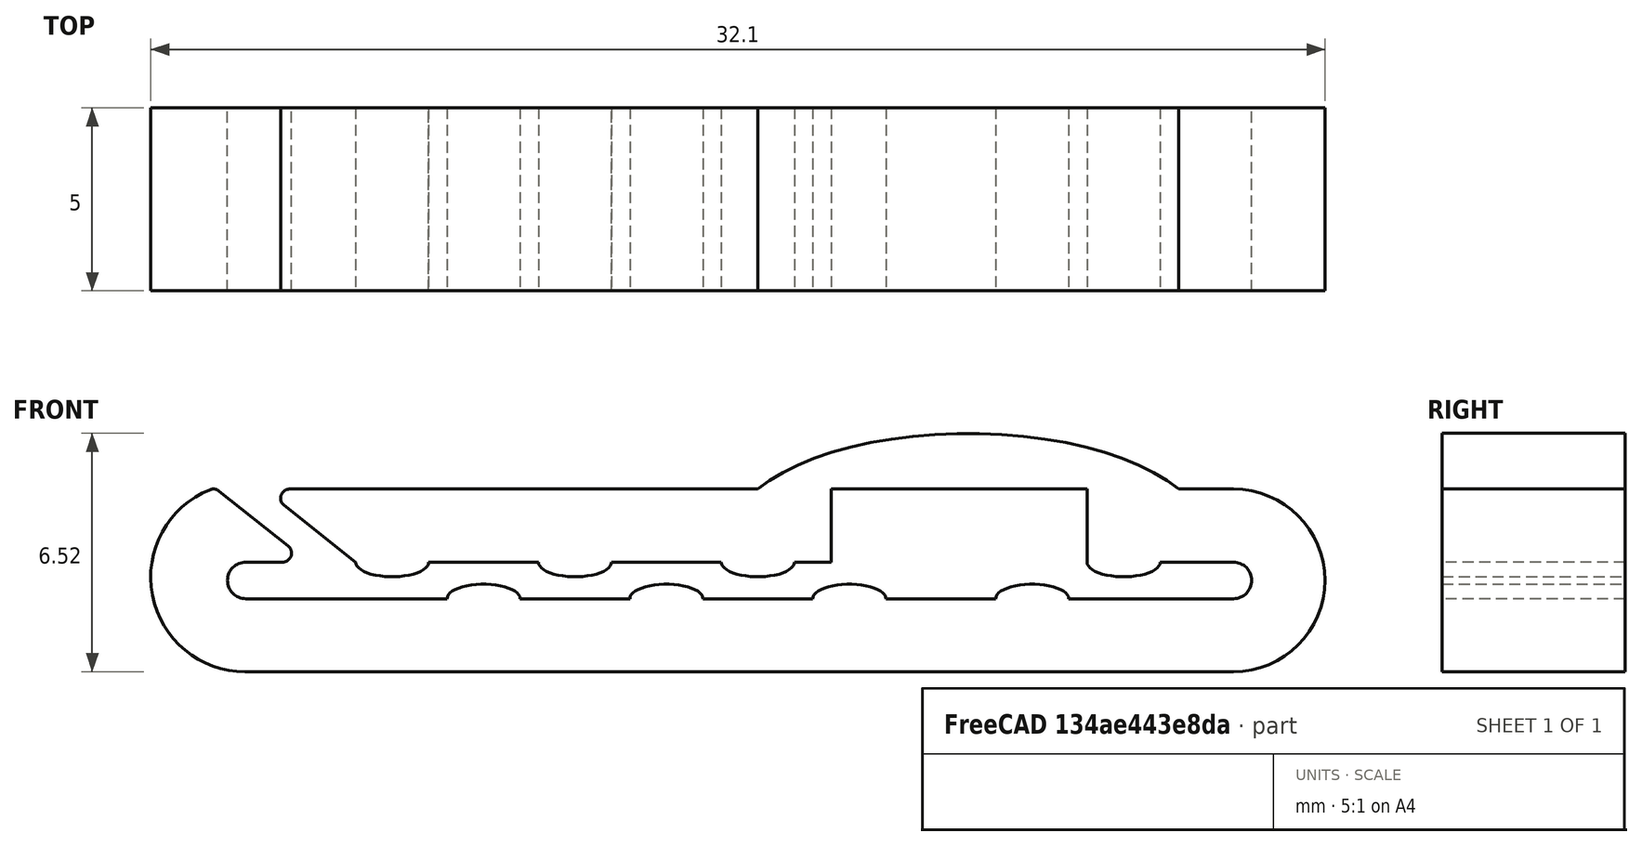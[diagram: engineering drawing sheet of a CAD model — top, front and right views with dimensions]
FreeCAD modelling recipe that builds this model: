
FCSTD DOCUMENT  (FreeCAD 2021.911R24301 +3846 (Git))
Label: BLTouch_Cable_Clamp
License: All rights reserved
LicenseURL: http://en.wikipedia.org/wiki/All_rights_reserved
objects: Sketcher::SketchObject×1, PartDesign::Pad×1, PartDesign::Body×1
note: 5 computed .brp shape members not serialized (recipe doc carries the construction recipe); baked Part::Feature solids carry a one-line shape summary decoded from their .brp

FEATURE [Sketcher::SketchObject] Sketch
  FullyConstrained = false
  MapMode = 5
  Placement = pos=(0,65.3,0) rot=(1,0,0;1.5708rad)
  sketch-geometry (56):
    g0: LineSegment StartX=62.4151 StartY=3.02512 StartZ=0 EndX=62.4151 EndY=5.02512 EndZ=0
    g1: LineSegment StartX=62.4151 StartY=5.02512 StartZ=0 EndX=55.4151 EndY=5.02512 EndZ=0
    g2: LineSegment StartX=55.4151 StartY=5.02512 StartZ=0 EndX=55.4151 EndY=3.02512 EndZ=0
    g3: LineSegment StartX=66.4151 StartY=2.02512 StartZ=0 EndX=61.9151 EndY=2.02512 EndZ=0
    g4: ArcOfEllipse CenterX=53.4151 CenterY=3.02512 CenterZ=0 NormalX=0 NormalY=0 NormalZ=1 MajorRadius=1 MinorRadius=0.4 AngleXU=-3.14159 StartAngle=0 EndAngle=3.14159
    g5: LineSegment [constr] StartX=52.4151 StartY=3.02512 StartZ=0 EndX=54.4151 EndY=3.02512 EndZ=0
    g6: LineSegment [constr] StartX=53.4151 StartY=2.62512 StartZ=0 EndX=53.4151 EndY=3.42512 EndZ=0
    g7: GeomPoint [constr] X=52.4986 Y=3.02512 Z=0
    g8: GeomPoint [constr] X=54.3317 Y=3.02512 Z=0
    g9: LineSegment StartX=55.4151 StartY=3.02512 StartZ=0 EndX=54.4151 EndY=3.02512 EndZ=0
    g10: ArcOfEllipse CenterX=60.9151 CenterY=2.02512 CenterZ=0 NormalX=0 NormalY=0 NormalZ=1 MajorRadius=1 MinorRadius=0.4 AngleXU=0 StartAngle=0 EndAngle=3.14159
    g11: LineSegment [constr] StartX=61.9151 StartY=2.02512 StartZ=0 EndX=59.9151 EndY=2.02512 EndZ=0
    g12: LineSegment [constr] StartX=60.9151 StartY=2.42512 StartZ=0 EndX=60.9151 EndY=1.62512 EndZ=0
    g13: GeomPoint [constr] X=61.8317 Y=2.02512 Z=0
    g14: GeomPoint [constr] X=59.9986 Y=2.02512 Z=0
    g15: ArcOfCircle CenterX=66.4151 CenterY=2.52512 CenterZ=0 NormalX=0 NormalY=0 NormalZ=1 AngleXU=0 Radius=0.5 StartAngle=4.71239 EndAngle=7.85398
    g16: LineSegment StartX=64.4151 StartY=3.02512 StartZ=0 EndX=66.4151 EndY=3.02512 EndZ=0
    g17: ArcOfEllipse CenterX=63.4151 CenterY=3.02512 CenterZ=0 NormalX=0 NormalY=0 NormalZ=1 MajorRadius=1 MinorRadius=0.4 AngleXU=-3.14159 StartAngle=0 EndAngle=3.14159
    g18: LineSegment [constr] StartX=62.4151 StartY=3.02512 StartZ=0 EndX=64.4151 EndY=3.02512 EndZ=0
    g19: LineSegment [constr] StartX=63.4151 StartY=2.62512 StartZ=0 EndX=63.4151 EndY=3.42512 EndZ=0
    g20: GeomPoint [constr] X=62.4986 Y=3.02512 Z=0
    g21: GeomPoint [constr] X=64.3317 Y=3.02512 Z=0
    g22: ArcOfEllipse CenterX=55.9151 CenterY=2.02512 CenterZ=0 NormalX=0 NormalY=0 NormalZ=1 MajorRadius=1 MinorRadius=0.4 AngleXU=0 StartAngle=0 EndAngle=3.14159
    g23: LineSegment [constr] StartX=56.9151 StartY=2.02512 StartZ=0 EndX=54.9151 EndY=2.02512 EndZ=0
    g24: LineSegment [constr] StartX=55.9151 StartY=2.42512 StartZ=0 EndX=55.9151 EndY=1.62512 EndZ=0
    g25: GeomPoint [constr] X=56.8317 Y=2.02512 Z=0
    g26: GeomPoint [constr] X=54.9986 Y=2.02512 Z=0
    g27: LineSegment StartX=59.9151 StartY=2.02512 StartZ=0 EndX=56.9151 EndY=2.02512 EndZ=0
    g28: ArcOfEllipse CenterX=50.9151 CenterY=2.02512 CenterZ=0 NormalX=0 NormalY=0 NormalZ=1 MajorRadius=1 MinorRadius=0.4 AngleXU=9.7e-15 StartAngle=-2.4e-14 EndAngle=3.14159
    g29: ArcOfEllipse CenterX=48.4152 CenterY=3.02512 CenterZ=0 NormalX=0 NormalY=0 NormalZ=1 MajorRadius=1 MinorRadius=0.4 AngleXU=3.14026 StartAngle=0.00332801 EndAngle=3.14492
    g30: ArcOfEllipse CenterX=45.9151 CenterY=2.02512 CenterZ=0 NormalX=0 NormalY=0 NormalZ=1 MajorRadius=1 MinorRadius=0.4 AngleXU=-1.9e-15 StartAngle=4.4e-15 EndAngle=3.14159
    g31: ArcOfEllipse CenterX=43.4152 CenterY=3.02512 CenterZ=0 NormalX=0 NormalY=0 NormalZ=1 MajorRadius=1 MinorRadius=0.4 AngleXU=3.14031 StartAngle=0.0032176 EndAngle=3.14481
    g32: LineSegment StartX=52.4151 StartY=3.02512 StartZ=0 EndX=49.4151 EndY=3.02512 EndZ=0
    g33: LineSegment StartX=54.9151 StartY=2.02512 StartZ=0 EndX=51.9151 EndY=2.02512 EndZ=0
    g34: LineSegment StartX=49.9151 StartY=2.02512 StartZ=0 EndX=46.9151 EndY=2.02512 EndZ=0
    g35: LineSegment StartX=47.4152 StartY=3.02512 StartZ=0 EndX=44.4152 EndY=3.02512 EndZ=0
    g36: ArcOfCircle CenterX=66.4151 CenterY=2.52512 CenterZ=0 NormalX=0 NormalY=0 NormalZ=1 AngleXU=0 Radius=2.5 StartAngle=4.71239 EndAngle=7.85398
    g37: LineSegment StartX=66.4151 StartY=0.02512 StartZ=0 EndX=39.3992 EndY=0.02512 EndZ=0
    g38: ArcOfEllipse CenterX=59.1651 CenterY=3.61512 CenterZ=0 NormalX=0 NormalY=0 NormalZ=1 MajorRadius=6.5578 MinorRadius=2.93247 AngleXU=0 StartAngle=0.501593 EndAngle=2.64
    g39: LineSegment [constr] StartX=65.723 StartY=3.61512 StartZ=0 EndX=52.6073 EndY=3.61512 EndZ=0
    g40: LineSegment [constr] StartX=59.1651 StartY=6.54759 StartZ=0 EndX=59.1651 EndY=0.682647 EndZ=0
    g41: GeomPoint [constr] X=65.0308 Y=3.61512 Z=0
    g42: GeomPoint [constr] X=53.2995 Y=3.61512 Z=0
    g43: LineSegment StartX=64.9151 StartY=5.02512 StartZ=0 EndX=66.4151 EndY=5.02512 EndZ=0
    g44: LineSegment StartX=53.4151 StartY=5.02512 StartZ=0 EndX=40.616 EndY=5.02512 EndZ=0
    g45: LineSegment StartX=39.4151 StartY=2.02512 StartZ=0 EndX=41.7849 EndY=2.02512 EndZ=0
    g46: LineSegment StartX=38.6843 StartY=4.9708 StartZ=0 EndX=40.5707 EndY=3.4708 EndZ=0
    g47: LineSegment StartX=40.4604 StartY=4.57944 StartZ=0 EndX=42.4152 EndY=3.02512 EndZ=0
    g48: LineSegment StartX=39.4151 StartY=3.02512 StartZ=0 EndX=40.4151 EndY=3.02512 EndZ=0
    g49: ArcOfCircle CenterX=40.4151 CenterY=3.27512 CenterZ=0 NormalX=0 NormalY=0 NormalZ=1 AngleXU=0 Radius=0.25 StartAngle=4.71239 EndAngle=7.1822
    g50: ArcOfCircle CenterX=39.4151 CenterY=2.52512 CenterZ=0 NormalX=0 NormalY=0 NormalZ=1 AngleXU=0 Radius=0.5 StartAngle=1.5708 EndAngle=4.71239
    g51: ArcOfCircle CenterX=40.616 CenterY=4.77512 CenterZ=0 NormalX=0 NormalY=0 NormalZ=1 AngleXU=0 Radius=0.25 StartAngle=1.5708 EndAngle=4.04061
    g52: LineSegment StartX=41.7849 StartY=2.02512 StartZ=0 EndX=44.9151 EndY=2.02512 EndZ=0
    g53: LineSegment [constr] StartX=40.616 StartY=5.02512 StartZ=0 EndX=36.2822 EndY=5.02512 EndZ=0
    g54: ArcOfCircle CenterX=38.5287 CenterY=4.77512 CenterZ=0 NormalX=0 NormalY=0 NormalZ=1 AngleXU=0 Radius=0.25 StartAngle=0.89902 EndAngle=1.95297
    g55: ArcOfCircle CenterX=39.3992 CenterY=2.60932 CenterZ=0 NormalX=0 NormalY=0 NormalZ=1 AngleXU=0 Radius=2.5842 StartAngle=1.95297 EndAngle=4.71239
  constraints (127):
    c: Vertical(g0)
    c: Coincident(g0,g1)
    c: Horizontal(g1)
    c: Coincident(g1,g2)
    c: Vertical(g2)
    c: Equal(g2,g0)
    c: Horizontal(g3)
    c: DistanceY(g3,g0) = 1
    c: DistanceY(g0,g0) = 2
    c: DistanceX(g0,g3) = 4
    c: DistanceX(g1,g1) = 7
    c: InternalAlignment(g5-g8 -> g4) x4
    c: Horizontal(g5)
    c: Coincident(g9,g2)
    c: Coincident(g9,g4)
    c: Horizontal(g9)
    c: DistanceX(g5,g5) = 2
    c: DistanceY(g6,g6) = 0.8
    c: InternalAlignment(g11-g14 -> g10) x4
    c: Coincident(g10,g3)
    c: DistanceX(g11,g11) = 2
    c: Horizontal(g11)
    c: DistanceY(g12,g12) = 0.8
    c: Coincident(g15,g3)
    c: Vertical(g15,g15)
    c: Vertical(g15,g3)
    c: Coincident(g16,g15)
    c: Horizontal(g16)
    c: Horizontal(g0,g16)
    c: Horizontal(g10,g11)
    c: Horizontal(g11,g3)
    c: InternalAlignment(g18-g21 -> g17) x4
    c: Horizontal(g18)
    c: DistanceX(g18,g18) = 2
    c: DistanceY(g19,g19) = 0.8
    c: Horizontal(g17,g17)
    c: Coincident(g17,g0)
    c: Coincident(g16,g17)
    c: DistanceX(g3,g3) = 4.5
    c: DistanceX(g9,g9) = 1
    c: InternalAlignment(g23-g26 -> g22) x4
    c: Horizontal(g23)
    c: Horizontal(g10,g22)
    c: Horizontal(g22,g22)
    c: Horizontal(g22,g22)
    c: DistanceX(g23,g23) = 2
    c: DistanceY(g24,g24) = 0.8
    c: Coincident(g10,g27)
    c: Coincident(g22,g27)
    c: DistanceX(g27,g27) = 3
    c: Horizontal(g4,g4)
    c: Horizontal(g4,g4)
    c: Horizontal(g28,g28)
    c: Horizontal(g28,g28)
    c: Horizontal(g29,g29)
    c: Horizontal(g29,g29)
    c: Horizontal(g30,g30)
    c: Horizontal(g30,g30)
    c: Horizontal(g31,g31)
    c: Horizontal(g31,g31)
    c: Horizontal(g28,g22)
    c: Equal(g22,g28)
    c: Equal(g4,g29)
    c: Equal(g28,g30)
    c: Equal(g29,g31)
    c: Horizontal(g30,g28)
    c: Horizontal(g4,g29)
    c: Horizontal(g29,g31)
    c: Coincident(g32,g4)
    c: Coincident(g32,g29)
    c: Coincident(g33,g22)
    c: Coincident(g33,g28)
    c: Coincident(g34,g28)
    c: Coincident(g34,g30)
    c: Coincident(g35,g29)
    c: Coincident(g35,g31)
    c: DistanceX(g33,g33) = 3
    c: Equal(g33,g32)
    c: Equal(g32,g34)
    c: Equal(g34,g35)
    c: DistanceX(g15) = 66.4151
    c: DistanceY(g15) = 2.52512
    c: Coincident(g36,g15)
    c: Vertical(g36,g15)
    c: Vertical(g15,g36)
    c: DistanceY(g36,g3) = 2
    c: Coincident(g37,g36)
    c: Horizontal(g37)
    c: InternalAlignment(g39-g42 -> g38) x4
    c: Horizontal(g39)
    c: Horizontal(g36,g38)
    c: Horizontal(g38,g38)
    c: Coincident(g43,g38)
    c: Horizontal(g43)
    c: DistanceX(g43,g43) = 1.5
    c: DistanceX(g38,g38) = 5.75
    c: DistanceY(g38,g38) = 1.41
    c: Coincident(g44,g38)
    c: Horizontal(g44)
    c: Horizontal(g45)
    c: Parallel(g46,g47)
    c: Horizontal(g48)
    c: Tangent(g46,g49) = 1.5708
    c: Tangent(g48,g49) = -1.5708
    c: Coincident(g50,g48)
    c: Coincident(g50,g45)
    c: Vertical(g48,g50)
    c: Vertical(g50,g45)
    c: DistanceY(g45,g48) = 1
    c: Diameter(g49) = 0.5
    c: Tangent(g44,g51) = -1.5708
    c: Tangent(g47,g51) = -1.5708
    c: Radius(g51) = 0.25
    c: DistanceX(g48,g48) = 1
    c: Coincident(g52,g45)
    c: Coincident(g52,g30)
    c: Horizontal(g52)
    c: DistanceX(g31) = 42.4152
    c: Coincident(g31,g47)
    c: Coincident(g53,g44)
    c: Horizontal(g53)
    c: DistanceX(g45,g30) = 5.5
    c: Tangent(g54,g46) = 1.5708
    c: Radius(g54) = 0.25
    c: Tangent(g54,g53)
    c: Tangent(g55,g37) = 1.5708
    c: Tangent(g55,g54) = -1.5708
FEATURE [PartDesign::Pad] Pad
  ClaimChildren = false
  Direction = (1,1,1)
  Fit = 0
  FitJoin = 0
  InnerFit = 0
  InnerFitJoin = 0
  InnerTaperAngle = 0
  InnerTaperAngleRev = 0
  Length = 5
  Length2 = 100
  Linearize = true
  NewSolid = false
  Placement = pos=(0,65.3,0) rot=(1,0,0;1.5708rad)
  Profile = -> Sketch
  Refine = true
  Suppress = false
  Type = 0
  _ProfileBasedVersion = 1
FEATURE [PartDesign::Body] Body  label="BLTouch_Cable_Clamp"
  AutoGroupSolids = false
  ExportMode = 0
  Group = -> [Sketch,Pad]
  Origin = -> Origin
  Tip = -> Pad
  _ExportChildren = -> [Pad]
  _GroupVersion = 1
